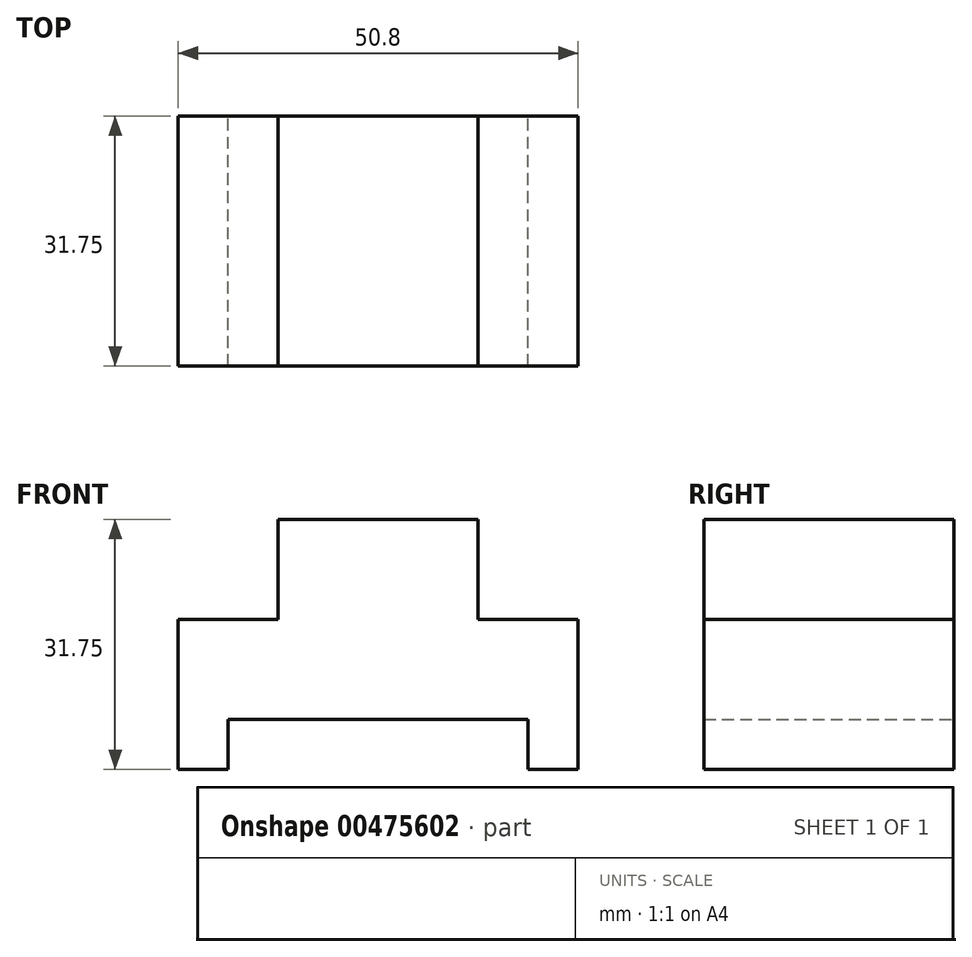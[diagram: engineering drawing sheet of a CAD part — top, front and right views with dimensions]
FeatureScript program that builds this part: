
annotation { "Feature Type Name" : "Feature", "Feature Type Description" : "" }
export const myFeature = defineFeature(function(context is Context, id is Id, definition is map)
    precondition{}
    {
        {
            var Q0;
            Q0=qCreatedBy(makeId("Front.planeOp"),FACE);
            var sketch = newSketch(context, id + "F0", { "sketchPlane" : qUnion([Q0])});
            skLineSegment(sketch, "E0", {"start": v(-31.77, -14.86) * mm, "end": v(-31.77, 4.2) * mm});
            skLineSegment(sketch, "E1", {"start": v(-31.77, 4.2) * mm, "end": v(-19.07, 4.2) * mm});
            skLineSegment(sketch, "E2", {"start": v(-19.07, 4.2) * mm, "end": v(-19.07, 16.9) * mm});
            skLineSegment(sketch, "E3", {"start": v(-19.07, 16.9) * mm, "end": v(6.33, 16.9) * mm});
            skLineSegment(sketch, "E4", {"start": v(6.33, 16.9) * mm, "end": v(6.33, 4.2) * mm});
            skLineSegment(sketch, "E5", {"start": v(6.33, 4.2) * mm, "end": v(19.03, 4.2) * mm});
            skLineSegment(sketch, "E6", {"start": v(19.03, 4.2) * mm, "end": v(19.03, -14.86) * mm});
            skLineSegment(sketch, "E7", {"start": v(19.03, -14.86) * mm, "end": v(12.68, -14.86) * mm});
            skLineSegment(sketch, "E8", {"start": v(12.68, -14.86) * mm, "end": v(12.68, -8.5) * mm});
            skLineSegment(sketch, "E9", {"start": v(12.68, -8.5) * mm, "end": v(-25.42, -8.5) * mm});
            skLineSegment(sketch, "E10", {"start": v(-25.42, -8.5) * mm, "end": v(-25.42, -14.86) * mm});
            skLineSegment(sketch, "E11", {"start": v(-25.42, -14.86) * mm, "end": v(-31.77, -14.86) * mm});
            skSolve(sketch);
        }
        {
            var Q0;
            Q0 = qSketchRegion(id + "F0", true);
            extrude(context, id + "F1", {"entities" : qUnion([Q0]), "depth" : 31.75 * mm});
        }
    });
